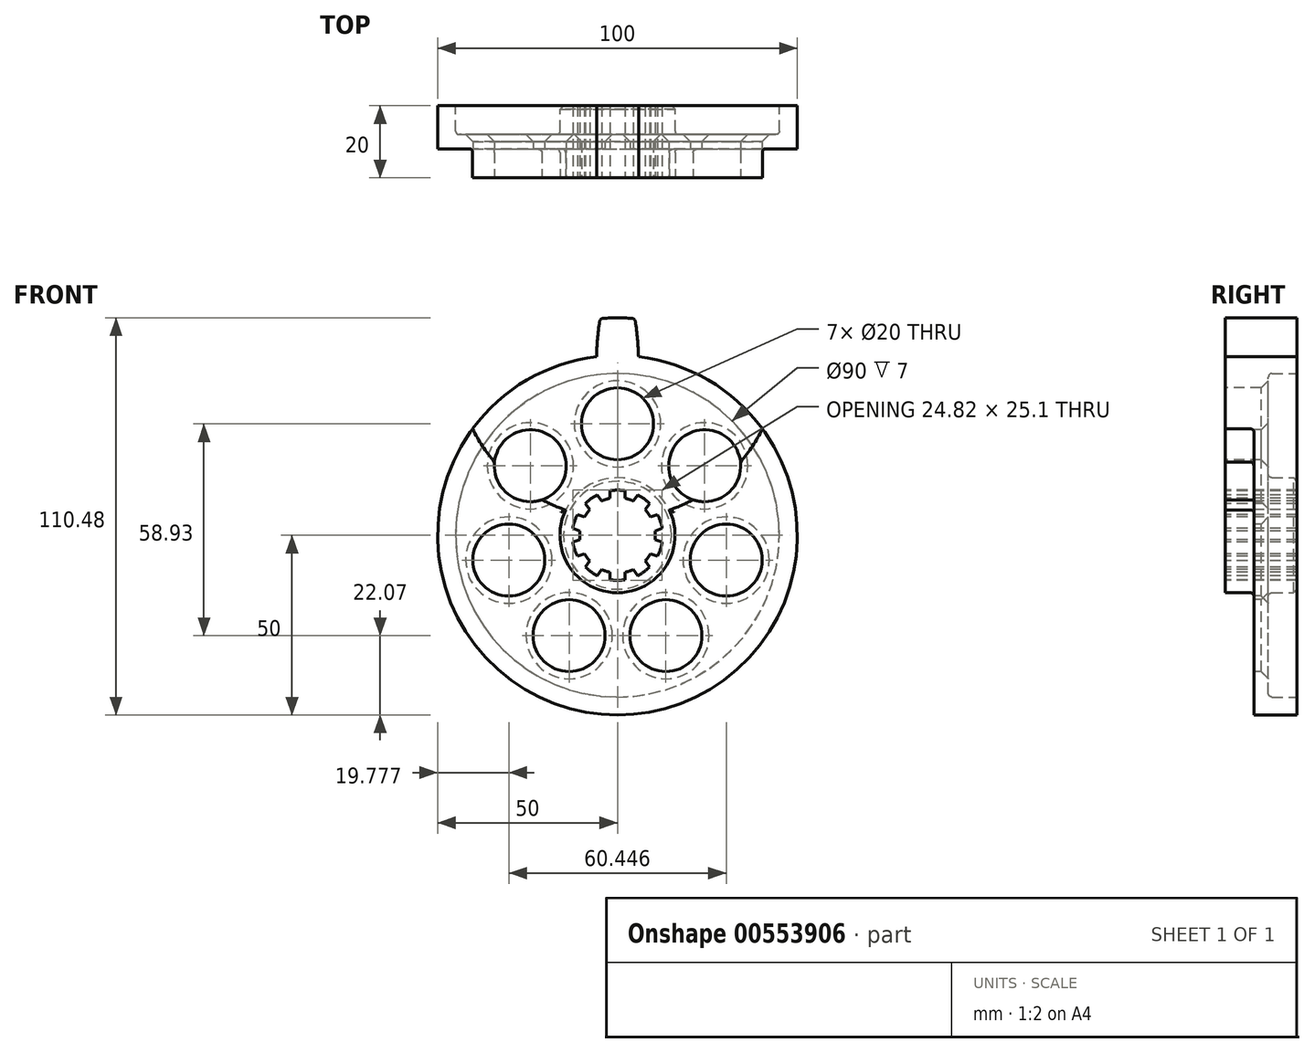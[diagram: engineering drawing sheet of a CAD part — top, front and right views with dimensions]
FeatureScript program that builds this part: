
annotation { "Feature Type Name" : "Feature", "Feature Type Description" : "" }
export const myFeature = defineFeature(function(context is Context, id is Id, definition is map)
    precondition{}
    {
        {
            var Q0;
            Q0=qCreatedBy(makeId("Front.planeOp"),FACE);
            var sketch = newSketch(context, id + "F0", { "sketchPlane" : qUnion([Q0])});
            skCircle(sketch, "E0", {"center": v(0, 0) * mm, "radius": 50 * mm});
            skLineSegment(sketch, "E1", {"start": v(-48.98, 46.5) * mm, "end": v(18.38, 46.5) * mm, "construction": true});
            skLineSegment(sketch, "E2", {"start": v(84.1, 97.1) * mm, "end": v(84.1, -36.75) * mm, "construction": true});
            skArc(sketch, "E3", {"start": v(-4.96, 59.5) * mm, "mid": v(-5.54, 54.59) * mm, "end": v(-5.84, 49.66) * mm});
            skArc(sketch, "E4.MirrorCS", {"start": v(4.96, 59.5) * mm, "mid": v(5.54, 54.59) * mm, "end": v(5.84, 49.66) * mm});
            skArc(sketch, "E5.trimOffspring", {"start": v(4.03, 60.35) * mm, "mid": v(0, 60.48) * mm, "end": v(-4.03, 60.35) * mm});
            skPoint(sketch, "E6.visualSharp", {"position": v(4.84, 60.29) * mm});
            skArc(sketch, "E6.filletArc", {"start": v(4.96, 59.5) * mm, "mid": v(4.65, 60.09) * mm, "end": v(4.03, 60.35) * mm});
            skPoint(sketch, "E7.visualSharp", {"position": v(-4.84, 60.29) * mm});
            skArc(sketch, "E7.filletArc", {"start": v(-4.03, 60.35) * mm, "mid": v(-4.65, 60.09) * mm, "end": v(-4.96, 59.5) * mm});
            skPoint(sketch, "E8.1.0", {"position": v(-54.63, -25.96) * mm});
            skArc(sketch, "E8.1.1", {"start": v(-54.28, -26.68) * mm, "mid": v(-52.38, -30.24) * mm, "end": v(-50.25, -33.67) * mm});
            skPoint(sketch, "E8.1.2", {"position": v(-49.8, -34.33) * mm});
            skArc(sketch, "E8.1.3", {"start": v(-54, -25.46) * mm, "mid": v(-50.04, -22.5) * mm, "end": v(-45.93, -19.77) * mm});
            skArc(sketch, "E8.1.4", {"start": v(-49.05, -34.04) * mm, "mid": v(-44.5, -32.09) * mm, "end": v(-40.08, -29.9) * mm});
            skArc(sketch, "E8.1.5", {"start": v(-50.25, -33.67) * mm, "mid": v(-49.71, -34.07) * mm, "end": v(-49.05, -34.04) * mm});
            skArc(sketch, "E8.1.6", {"start": v(-54, -25.46) * mm, "mid": v(-54.36, -26.02) * mm, "end": v(-54.28, -26.68) * mm});
            skPoint(sketch, "E8.2.0", {"position": v(49.8, -34.33) * mm});
            skArc(sketch, "E8.2.1", {"start": v(50.25, -33.67) * mm, "mid": v(52.38, -30.24) * mm, "end": v(54.28, -26.68) * mm});
            skPoint(sketch, "E8.2.2", {"position": v(54.63, -25.96) * mm});
            skArc(sketch, "E8.2.3", {"start": v(49.05, -34.04) * mm, "mid": v(44.5, -32.09) * mm, "end": v(40.08, -29.9) * mm});
            skArc(sketch, "E8.2.4", {"start": v(54, -25.46) * mm, "mid": v(50.04, -22.5) * mm, "end": v(45.93, -19.77) * mm});
            skArc(sketch, "E8.2.5", {"start": v(54.28, -26.68) * mm, "mid": v(54.36, -26.02) * mm, "end": v(54, -25.46) * mm});
            skArc(sketch, "E8.2.6", {"start": v(49.05, -34.04) * mm, "mid": v(49.71, -34.07) * mm, "end": v(50.25, -33.67) * mm});
            skSolve(sketch);
        }
        {
            var Q0;
            {var subQ0=sQuery(id+"F0.wireOp",EDGE,"E0");var subQ18=makeQuery(id+"F0.imprint","INTERSECT",VERTEX,{"derivedFrom":[subQ0,sQuery(id+"F0.wireOp",EDGE,"c62fa7f7-7299-4b17-82dd-0c70f37f38ce.11.0")]});Q0=makeQuery(id+"F0.imprint","IMPRINT",FACE,{"disambiguationData":[TD([[makeQuery(id+"F0.imprint","IMPRINT",EDGE,{"disambiguationData":[TD([[subQ18,-1.0]])],"derivedFrom":subQ0}),1.0]])]});}
            var Q1;
            {var subQ0=sQuery(id+"F0.wireOp",EDGE,"c62fa7f7-7299-4b17-82dd-0c70f37f38ce.1.0");Q1=makeQuery(id+"F0.imprint","IMPRINT",FACE,{"disambiguationData":[TD([[makeQuery(id+"F0.imprint","IMPRINT",EDGE,{"derivedFrom":subQ0}),1.0]])]});}
            var Q2;
            {var subQ0=sQuery(id+"F0.wireOp",EDGE,"E3");Q2=makeQuery(id+"F0.imprint","IMPRINT",FACE,{"disambiguationData":[TD([[makeQuery(id+"F0.imprint","IMPRINT",EDGE,{"derivedFrom":subQ0}),1.0]])]});}
            var Q3;
            {var subQ0=sQuery(id+"F0.wireOp",EDGE,"c62fa7f7-7299-4b17-82dd-0c70f37f38ce.14.0");Q3=makeQuery(id+"F0.imprint","IMPRINT",FACE,{"disambiguationData":[TD([[makeQuery(id+"F0.imprint","IMPRINT",EDGE,{"derivedFrom":subQ0}),1.0]])]});}
            var Q4;
            {var subQ0=sQuery(id+"F0.wireOp",EDGE,"c62fa7f7-7299-4b17-82dd-0c70f37f38ce.13.0");Q4=makeQuery(id+"F0.imprint","IMPRINT",FACE,{"disambiguationData":[TD([[makeQuery(id+"F0.imprint","IMPRINT",EDGE,{"derivedFrom":subQ0}),1.0]])]});}
            var Q5;
            {var subQ0=sQuery(id+"F0.wireOp",EDGE,"c62fa7f7-7299-4b17-82dd-0c70f37f38ce.12.0");Q5=makeQuery(id+"F0.imprint","IMPRINT",FACE,{"disambiguationData":[TD([[makeQuery(id+"F0.imprint","IMPRINT",EDGE,{"derivedFrom":subQ0}),1.0]])]});}
            var Q6;
            {var subQ0=sQuery(id+"F0.wireOp",EDGE,"c62fa7f7-7299-4b17-82dd-0c70f37f38ce.11.0");Q6=makeQuery(id+"F0.imprint","IMPRINT",FACE,{"disambiguationData":[TD([[makeQuery(id+"F0.imprint","IMPRINT",EDGE,{"derivedFrom":subQ0}),1.0]])]});}
            var Q7;
            {var subQ0=sQuery(id+"F0.wireOp",EDGE,"c62fa7f7-7299-4b17-82dd-0c70f37f38ce.10.0");Q7=makeQuery(id+"F0.imprint","IMPRINT",FACE,{"disambiguationData":[TD([[makeQuery(id+"F0.imprint","IMPRINT",EDGE,{"derivedFrom":subQ0}),1.0]])]});}
            var Q8;
            {var subQ0=sQuery(id+"F0.wireOp",EDGE,"c62fa7f7-7299-4b17-82dd-0c70f37f38ce.9.0");Q8=makeQuery(id+"F0.imprint","IMPRINT",FACE,{"disambiguationData":[TD([[makeQuery(id+"F0.imprint","IMPRINT",EDGE,{"derivedFrom":subQ0}),1.0]])]});}
            var Q9;
            {var subQ0=sQuery(id+"F0.wireOp",EDGE,"c62fa7f7-7299-4b17-82dd-0c70f37f38ce.8.0");Q9=makeQuery(id+"F0.imprint","IMPRINT",FACE,{"disambiguationData":[TD([[makeQuery(id+"F0.imprint","IMPRINT",EDGE,{"derivedFrom":subQ0}),1.0]])]});}
            var Q10;
            {var subQ0=sQuery(id+"F0.wireOp",EDGE,"c62fa7f7-7299-4b17-82dd-0c70f37f38ce.7.0");Q10=makeQuery(id+"F0.imprint","IMPRINT",FACE,{"disambiguationData":[TD([[makeQuery(id+"F0.imprint","IMPRINT",EDGE,{"derivedFrom":subQ0}),1.0]])]});}
            var Q11;
            {var subQ0=sQuery(id+"F0.wireOp",EDGE,"c62fa7f7-7299-4b17-82dd-0c70f37f38ce.6.0");Q11=makeQuery(id+"F0.imprint","IMPRINT",FACE,{"disambiguationData":[TD([[makeQuery(id+"F0.imprint","IMPRINT",EDGE,{"derivedFrom":subQ0}),1.0]])]});}
            var Q12;
            {var subQ0=sQuery(id+"F0.wireOp",EDGE,"c62fa7f7-7299-4b17-82dd-0c70f37f38ce.5.0");Q12=makeQuery(id+"F0.imprint","IMPRINT",FACE,{"disambiguationData":[TD([[makeQuery(id+"F0.imprint","IMPRINT",EDGE,{"derivedFrom":subQ0}),1.0]])]});}
            var Q13;
            {var subQ0=sQuery(id+"F0.wireOp",EDGE,"c62fa7f7-7299-4b17-82dd-0c70f37f38ce.4.0");Q13=makeQuery(id+"F0.imprint","IMPRINT",FACE,{"disambiguationData":[TD([[makeQuery(id+"F0.imprint","IMPRINT",EDGE,{"derivedFrom":subQ0}),1.0]])]});}
            var Q14;
            {var subQ0=sQuery(id+"F0.wireOp",EDGE,"c62fa7f7-7299-4b17-82dd-0c70f37f38ce.3.0");Q14=makeQuery(id+"F0.imprint","IMPRINT",FACE,{"disambiguationData":[TD([[makeQuery(id+"F0.imprint","IMPRINT",EDGE,{"derivedFrom":subQ0}),1.0]])]});}
            var Q15;
            {var subQ0=sQuery(id+"F0.wireOp",EDGE,"c62fa7f7-7299-4b17-82dd-0c70f37f38ce.2.0");Q15=makeQuery(id+"F0.imprint","IMPRINT",FACE,{"disambiguationData":[TD([[makeQuery(id+"F0.imprint","IMPRINT",EDGE,{"derivedFrom":subQ0}),1.0]])]});}
            extrude(context, id + "F1", {"entities" : qUnion([Q0, Q1, Q2, Q3, Q4, Q5, Q6, Q7, Q8, Q9, Q10, Q11, Q12, Q13, Q14, Q15]), "depth" : 20 * mm, "offsetDistance" : 25 * mm});
        }
        {
            var Q0;
            Q0=makeQuery(id+"F1.opExtrude","CAP_FACE",FACE,{"disambiguationData":[OSD([sQuery(id+"F0.wireOp",EDGE,"E0"),sQuery(id+"F0.wireOp",EDGE,"E3"),sQuery(id+"F0.wireOp",EDGE,"E4.MirrorCS"),sQuery(id+"F0.wireOp",EDGE,"E5.trimOffspring"),sQuery(id+"F0.wireOp",EDGE,"c62fa7f7-7299-4b17-82dd-0c70f37f38ce.1.0"),sQuery(id+"F0.wireOp",EDGE,"c62fa7f7-7299-4b17-82dd-0c70f37f38ce.1.1"),sQuery(id+"F0.wireOp",EDGE,"c62fa7f7-7299-4b17-82dd-0c70f37f38ce.1.2"),sQuery(id+"F0.wireOp",EDGE,"c62fa7f7-7299-4b17-82dd-0c70f37f38ce.2.0"),sQuery(id+"F0.wireOp",EDGE,"c62fa7f7-7299-4b17-82dd-0c70f37f38ce.2.1"),sQuery(id+"F0.wireOp",EDGE,"c62fa7f7-7299-4b17-82dd-0c70f37f38ce.2.2"),sQuery(id+"F0.wireOp",EDGE,"c62fa7f7-7299-4b17-82dd-0c70f37f38ce.3.0"),sQuery(id+"F0.wireOp",EDGE,"c62fa7f7-7299-4b17-82dd-0c70f37f38ce.3.1"),sQuery(id+"F0.wireOp",EDGE,"c62fa7f7-7299-4b17-82dd-0c70f37f38ce.3.2"),sQuery(id+"F0.wireOp",EDGE,"c62fa7f7-7299-4b17-82dd-0c70f37f38ce.4.0"),sQuery(id+"F0.wireOp",EDGE,"c62fa7f7-7299-4b17-82dd-0c70f37f38ce.4.1"),sQuery(id+"F0.wireOp",EDGE,"c62fa7f7-7299-4b17-82dd-0c70f37f38ce.4.2"),sQuery(id+"F0.wireOp",EDGE,"c62fa7f7-7299-4b17-82dd-0c70f37f38ce.5.0"),sQuery(id+"F0.wireOp",EDGE,"c62fa7f7-7299-4b17-82dd-0c70f37f38ce.5.1"),sQuery(id+"F0.wireOp",EDGE,"c62fa7f7-7299-4b17-82dd-0c70f37f38ce.5.2"),sQuery(id+"F0.wireOp",EDGE,"c62fa7f7-7299-4b17-82dd-0c70f37f38ce.6.0"),sQuery(id+"F0.wireOp",EDGE,"c62fa7f7-7299-4b17-82dd-0c70f37f38ce.6.1"),sQuery(id+"F0.wireOp",EDGE,"c62fa7f7-7299-4b17-82dd-0c70f37f38ce.6.2"),sQuery(id+"F0.wireOp",EDGE,"c62fa7f7-7299-4b17-82dd-0c70f37f38ce.7.0"),sQuery(id+"F0.wireOp",EDGE,"c62fa7f7-7299-4b17-82dd-0c70f37f38ce.7.1"),sQuery(id+"F0.wireOp",EDGE,"c62fa7f7-7299-4b17-82dd-0c70f37f38ce.7.2"),sQuery(id+"F0.wireOp",EDGE,"c62fa7f7-7299-4b17-82dd-0c70f37f38ce.8.0"),sQuery(id+"F0.wireOp",EDGE,"c62fa7f7-7299-4b17-82dd-0c70f37f38ce.8.1"),sQuery(id+"F0.wireOp",EDGE,"c62fa7f7-7299-4b17-82dd-0c70f37f38ce.8.2"),sQuery(id+"F0.wireOp",EDGE,"c62fa7f7-7299-4b17-82dd-0c70f37f38ce.9.0"),sQuery(id+"F0.wireOp",EDGE,"c62fa7f7-7299-4b17-82dd-0c70f37f38ce.9.1"),sQuery(id+"F0.wireOp",EDGE,"c62fa7f7-7299-4b17-82dd-0c70f37f38ce.9.2"),sQuery(id+"F0.wireOp",EDGE,"c62fa7f7-7299-4b17-82dd-0c70f37f38ce.10.0"),sQuery(id+"F0.wireOp",EDGE,"c62fa7f7-7299-4b17-82dd-0c70f37f38ce.10.1"),sQuery(id+"F0.wireOp",EDGE,"c62fa7f7-7299-4b17-82dd-0c70f37f38ce.10.2"),sQuery(id+"F0.wireOp",EDGE,"c62fa7f7-7299-4b17-82dd-0c70f37f38ce.11.0"),sQuery(id+"F0.wireOp",EDGE,"c62fa7f7-7299-4b17-82dd-0c70f37f38ce.11.1"),sQuery(id+"F0.wireOp",EDGE,"c62fa7f7-7299-4b17-82dd-0c70f37f38ce.11.2"),sQuery(id+"F0.wireOp",EDGE,"c62fa7f7-7299-4b17-82dd-0c70f37f38ce.12.0"),sQuery(id+"F0.wireOp",EDGE,"c62fa7f7-7299-4b17-82dd-0c70f37f38ce.12.1"),sQuery(id+"F0.wireOp",EDGE,"c62fa7f7-7299-4b17-82dd-0c70f37f38ce.12.2"),sQuery(id+"F0.wireOp",EDGE,"c62fa7f7-7299-4b17-82dd-0c70f37f38ce.13.0"),sQuery(id+"F0.wireOp",EDGE,"c62fa7f7-7299-4b17-82dd-0c70f37f38ce.13.1"),sQuery(id+"F0.wireOp",EDGE,"c62fa7f7-7299-4b17-82dd-0c70f37f38ce.13.2"),sQuery(id+"F0.wireOp",EDGE,"c62fa7f7-7299-4b17-82dd-0c70f37f38ce.14.0"),sQuery(id+"F0.wireOp",EDGE,"c62fa7f7-7299-4b17-82dd-0c70f37f38ce.14.1"),sQuery(id+"F0.wireOp",EDGE,"c62fa7f7-7299-4b17-82dd-0c70f37f38ce.14.2")])],"isStart":false});
            var sketch = newSketch(context, id + "F2", { "sketchPlane" : qUnion([Q0])});
            skCircle(sketch, "E9", {"center": v(0, 0) * mm, "radius": 10.5 * mm});
            skArc(sketch, "E10", {"start": v(2.05, 12.38) * mm, "mid": v(0, 12.55) * mm, "end": v(-2.05, 12.38) * mm});
            skLineSegment(sketch, "E11", {"start": v(-2.05, 12.38) * mm, "end": v(-2.05, 10.3) * mm});
            skLineSegment(sketch, "E12", {"start": v(2.05, 12.38) * mm, "end": v(2.05, 10.3) * mm});
            skLineSegment(sketch, "E13.1.0", {"start": v(-8.94, 8.81) * mm, "end": v(-7.71, 7.13) * mm});
            skArc(sketch, "E13.1.1", {"start": v(-5.62, 11.22) * mm, "mid": v(-7.38, 10.15) * mm, "end": v(-8.94, 8.81) * mm});
            skLineSegment(sketch, "E13.1.2", {"start": v(-5.62, 11.22) * mm, "end": v(-4.4, 9.54) * mm});
            skLineSegment(sketch, "E13.2.0", {"start": v(-12.4, 1.88) * mm, "end": v(-10.43, 1.23) * mm});
            skArc(sketch, "E13.2.1", {"start": v(-11.14, 5.78) * mm, "mid": v(-11.94, 3.88) * mm, "end": v(-12.4, 1.88) * mm});
            skLineSegment(sketch, "E13.2.2", {"start": v(-11.14, 5.78) * mm, "end": v(-9.16, 5.13) * mm});
            skLineSegment(sketch, "E13.3.0", {"start": v(-11.14, -5.78) * mm, "end": v(-9.16, -5.13) * mm});
            skArc(sketch, "E13.3.1", {"start": v(-12.4, -1.88) * mm, "mid": v(-11.94, -3.88) * mm, "end": v(-11.14, -5.78) * mm});
            skLineSegment(sketch, "E13.3.2", {"start": v(-12.4, -1.88) * mm, "end": v(-10.43, -1.23) * mm});
            skLineSegment(sketch, "E13.4.0", {"start": v(-5.62, -11.22) * mm, "end": v(-4.4, -9.54) * mm});
            skArc(sketch, "E13.4.1", {"start": v(-8.94, -8.81) * mm, "mid": v(-7.38, -10.15) * mm, "end": v(-5.62, -11.22) * mm});
            skLineSegment(sketch, "E13.4.2", {"start": v(-8.94, -8.81) * mm, "end": v(-7.71, -7.13) * mm});
            skLineSegment(sketch, "E13.5.0", {"start": v(2.05, -12.38) * mm, "end": v(2.05, -10.3) * mm});
            skArc(sketch, "E13.5.1", {"start": v(-2.05, -12.38) * mm, "mid": v(0, -12.55) * mm, "end": v(2.05, -12.38) * mm});
            skLineSegment(sketch, "E13.5.2", {"start": v(-2.05, -12.38) * mm, "end": v(-2.05, -10.3) * mm});
            skLineSegment(sketch, "E13.6.0", {"start": v(8.94, -8.81) * mm, "end": v(7.71, -7.13) * mm});
            skArc(sketch, "E13.6.1", {"start": v(5.62, -11.22) * mm, "mid": v(7.38, -10.15) * mm, "end": v(8.94, -8.81) * mm});
            skLineSegment(sketch, "E13.6.2", {"start": v(5.62, -11.22) * mm, "end": v(4.4, -9.54) * mm});
            skLineSegment(sketch, "E13.7.0", {"start": v(12.4, -1.88) * mm, "end": v(10.43, -1.23) * mm});
            skArc(sketch, "E13.7.1", {"start": v(11.14, -5.78) * mm, "mid": v(11.94, -3.88) * mm, "end": v(12.4, -1.88) * mm});
            skLineSegment(sketch, "E13.7.2", {"start": v(11.14, -5.78) * mm, "end": v(9.16, -5.13) * mm});
            skLineSegment(sketch, "E13.8.0", {"start": v(11.14, 5.78) * mm, "end": v(9.16, 5.13) * mm});
            skArc(sketch, "E13.8.1", {"start": v(12.4, 1.88) * mm, "mid": v(11.94, 3.88) * mm, "end": v(11.14, 5.78) * mm});
            skLineSegment(sketch, "E13.8.2", {"start": v(12.4, 1.88) * mm, "end": v(10.43, 1.23) * mm});
            skLineSegment(sketch, "E13.9.0", {"start": v(5.62, 11.22) * mm, "end": v(4.4, 9.54) * mm});
            skArc(sketch, "E13.9.1", {"start": v(8.94, 8.81) * mm, "mid": v(7.38, 10.15) * mm, "end": v(5.62, 11.22) * mm});
            skLineSegment(sketch, "E13.9.2", {"start": v(8.94, 8.81) * mm, "end": v(7.71, 7.13) * mm});
            skSolve(sketch);
        }
        {
            var Q0;
            {var subQ0=sQuery(id+"F2.wireOp",EDGE,"E9");var subQ8=makeQuery(id+"F2.imprint","INTERSECT",VERTEX,{"derivedFrom":[subQ0,sQuery(id+"F2.wireOp",EDGE,"E13.8.0")]});Q0=makeQuery(id+"F2.imprint","IMPRINT",FACE,{"disambiguationData":[TD([[makeQuery(id+"F2.imprint","IMPRINT",EDGE,{"disambiguationData":[TD([[subQ8,1.0]])],"derivedFrom":subQ0}),1.0]])]});}
            var Q1;
            {var subQ0=sQuery(id+"F2.wireOp",EDGE,"E13.1.0");Q1=makeQuery(id+"F2.imprint","IMPRINT",FACE,{"disambiguationData":[TD([[makeQuery(id+"F2.imprint","IMPRINT",EDGE,{"derivedFrom":subQ0}),1.0]])]});}
            var Q2;
            Q2=makeQuery(id+"F2.imprint","IMPRINT",FACE,{"disambiguationData":[TD([[makeQuery(id+"F2.imprint","IMPRINT",EDGE,{"derivedFrom":sQuery(id+"F2.wireOp",EDGE,"E10")}),1.0]])]});
            var Q3;
            {var subQ0=sQuery(id+"F2.wireOp",EDGE,"E13.9.0");Q3=makeQuery(id+"F2.imprint","IMPRINT",FACE,{"disambiguationData":[TD([[makeQuery(id+"F2.imprint","IMPRINT",EDGE,{"derivedFrom":subQ0}),1.0]])]});}
            var Q4;
            {var subQ0=sQuery(id+"F2.wireOp",EDGE,"E13.2.0");Q4=makeQuery(id+"F2.imprint","IMPRINT",FACE,{"disambiguationData":[TD([[makeQuery(id+"F2.imprint","IMPRINT",EDGE,{"derivedFrom":subQ0}),1.0]])]});}
            var Q5;
            {var subQ0=sQuery(id+"F2.wireOp",EDGE,"E13.3.0");Q5=makeQuery(id+"F2.imprint","IMPRINT",FACE,{"disambiguationData":[TD([[makeQuery(id+"F2.imprint","IMPRINT",EDGE,{"derivedFrom":subQ0}),1.0]])]});}
            var Q6;
            {var subQ0=sQuery(id+"F2.wireOp",EDGE,"E13.4.0");Q6=makeQuery(id+"F2.imprint","IMPRINT",FACE,{"disambiguationData":[TD([[makeQuery(id+"F2.imprint","IMPRINT",EDGE,{"derivedFrom":subQ0}),1.0]])]});}
            var Q7;
            {var subQ0=sQuery(id+"F2.wireOp",EDGE,"E13.5.0");Q7=makeQuery(id+"F2.imprint","IMPRINT",FACE,{"disambiguationData":[TD([[makeQuery(id+"F2.imprint","IMPRINT",EDGE,{"derivedFrom":subQ0}),1.0]])]});}
            var Q8;
            {var subQ0=sQuery(id+"F2.wireOp",EDGE,"E13.6.0");Q8=makeQuery(id+"F2.imprint","IMPRINT",FACE,{"disambiguationData":[TD([[makeQuery(id+"F2.imprint","IMPRINT",EDGE,{"derivedFrom":subQ0}),1.0]])]});}
            var Q9;
            {var subQ0=sQuery(id+"F2.wireOp",EDGE,"E13.7.0");Q9=makeQuery(id+"F2.imprint","IMPRINT",FACE,{"disambiguationData":[TD([[makeQuery(id+"F2.imprint","IMPRINT",EDGE,{"derivedFrom":subQ0}),1.0]])]});}
            var Q10;
            {var subQ0=sQuery(id+"F2.wireOp",EDGE,"E13.8.0");Q10=makeQuery(id+"F2.imprint","IMPRINT",FACE,{"disambiguationData":[TD([[makeQuery(id+"F2.imprint","IMPRINT",EDGE,{"derivedFrom":subQ0}),1.0]])]});}
            extrude(context, id + "F3", {"entities" : qUnion([Q0, Q1, Q2, Q3, Q4, Q5, Q6, Q7, Q8, Q9, Q10]), "operationType" : NewBodyOperationType.REMOVE, "oppositeDirection" : true, "depth" : 20 * mm, "offsetDistance" : 25 * mm});
        }
        {
            var Q0;
            Q0=makeQuery(id+"F1.opExtrude","CAP_FACE",FACE,{"disambiguationData":[OSD([sQuery(id+"F0.wireOp",EDGE,"E0"),sQuery(id+"F0.wireOp",EDGE,"E3"),sQuery(id+"F0.wireOp",EDGE,"E4.MirrorCS"),sQuery(id+"F0.wireOp",EDGE,"E5.trimOffspring"),sQuery(id+"F0.wireOp",EDGE,"c62fa7f7-7299-4b17-82dd-0c70f37f38ce.1.0"),sQuery(id+"F0.wireOp",EDGE,"c62fa7f7-7299-4b17-82dd-0c70f37f38ce.1.1"),sQuery(id+"F0.wireOp",EDGE,"c62fa7f7-7299-4b17-82dd-0c70f37f38ce.1.2"),sQuery(id+"F0.wireOp",EDGE,"c62fa7f7-7299-4b17-82dd-0c70f37f38ce.2.0"),sQuery(id+"F0.wireOp",EDGE,"c62fa7f7-7299-4b17-82dd-0c70f37f38ce.2.1"),sQuery(id+"F0.wireOp",EDGE,"c62fa7f7-7299-4b17-82dd-0c70f37f38ce.2.2"),sQuery(id+"F0.wireOp",EDGE,"c62fa7f7-7299-4b17-82dd-0c70f37f38ce.3.0"),sQuery(id+"F0.wireOp",EDGE,"c62fa7f7-7299-4b17-82dd-0c70f37f38ce.3.1"),sQuery(id+"F0.wireOp",EDGE,"c62fa7f7-7299-4b17-82dd-0c70f37f38ce.3.2"),sQuery(id+"F0.wireOp",EDGE,"c62fa7f7-7299-4b17-82dd-0c70f37f38ce.4.0"),sQuery(id+"F0.wireOp",EDGE,"c62fa7f7-7299-4b17-82dd-0c70f37f38ce.4.1"),sQuery(id+"F0.wireOp",EDGE,"c62fa7f7-7299-4b17-82dd-0c70f37f38ce.4.2"),sQuery(id+"F0.wireOp",EDGE,"c62fa7f7-7299-4b17-82dd-0c70f37f38ce.5.0"),sQuery(id+"F0.wireOp",EDGE,"c62fa7f7-7299-4b17-82dd-0c70f37f38ce.5.1"),sQuery(id+"F0.wireOp",EDGE,"c62fa7f7-7299-4b17-82dd-0c70f37f38ce.5.2"),sQuery(id+"F0.wireOp",EDGE,"c62fa7f7-7299-4b17-82dd-0c70f37f38ce.6.0"),sQuery(id+"F0.wireOp",EDGE,"c62fa7f7-7299-4b17-82dd-0c70f37f38ce.6.1"),sQuery(id+"F0.wireOp",EDGE,"c62fa7f7-7299-4b17-82dd-0c70f37f38ce.6.2"),sQuery(id+"F0.wireOp",EDGE,"c62fa7f7-7299-4b17-82dd-0c70f37f38ce.7.0"),sQuery(id+"F0.wireOp",EDGE,"c62fa7f7-7299-4b17-82dd-0c70f37f38ce.7.1"),sQuery(id+"F0.wireOp",EDGE,"c62fa7f7-7299-4b17-82dd-0c70f37f38ce.7.2"),sQuery(id+"F0.wireOp",EDGE,"c62fa7f7-7299-4b17-82dd-0c70f37f38ce.8.0"),sQuery(id+"F0.wireOp",EDGE,"c62fa7f7-7299-4b17-82dd-0c70f37f38ce.8.1"),sQuery(id+"F0.wireOp",EDGE,"c62fa7f7-7299-4b17-82dd-0c70f37f38ce.8.2"),sQuery(id+"F0.wireOp",EDGE,"c62fa7f7-7299-4b17-82dd-0c70f37f38ce.9.0"),sQuery(id+"F0.wireOp",EDGE,"c62fa7f7-7299-4b17-82dd-0c70f37f38ce.9.1"),sQuery(id+"F0.wireOp",EDGE,"c62fa7f7-7299-4b17-82dd-0c70f37f38ce.9.2"),sQuery(id+"F0.wireOp",EDGE,"c62fa7f7-7299-4b17-82dd-0c70f37f38ce.10.0"),sQuery(id+"F0.wireOp",EDGE,"c62fa7f7-7299-4b17-82dd-0c70f37f38ce.10.1"),sQuery(id+"F0.wireOp",EDGE,"c62fa7f7-7299-4b17-82dd-0c70f37f38ce.10.2"),sQuery(id+"F0.wireOp",EDGE,"c62fa7f7-7299-4b17-82dd-0c70f37f38ce.11.0"),sQuery(id+"F0.wireOp",EDGE,"c62fa7f7-7299-4b17-82dd-0c70f37f38ce.11.1"),sQuery(id+"F0.wireOp",EDGE,"c62fa7f7-7299-4b17-82dd-0c70f37f38ce.11.2"),sQuery(id+"F0.wireOp",EDGE,"c62fa7f7-7299-4b17-82dd-0c70f37f38ce.12.0"),sQuery(id+"F0.wireOp",EDGE,"c62fa7f7-7299-4b17-82dd-0c70f37f38ce.12.1"),sQuery(id+"F0.wireOp",EDGE,"c62fa7f7-7299-4b17-82dd-0c70f37f38ce.12.2"),sQuery(id+"F0.wireOp",EDGE,"c62fa7f7-7299-4b17-82dd-0c70f37f38ce.13.0"),sQuery(id+"F0.wireOp",EDGE,"c62fa7f7-7299-4b17-82dd-0c70f37f38ce.13.1"),sQuery(id+"F0.wireOp",EDGE,"c62fa7f7-7299-4b17-82dd-0c70f37f38ce.13.2"),sQuery(id+"F0.wireOp",EDGE,"c62fa7f7-7299-4b17-82dd-0c70f37f38ce.14.0"),sQuery(id+"F0.wireOp",EDGE,"c62fa7f7-7299-4b17-82dd-0c70f37f38ce.14.1"),sQuery(id+"F0.wireOp",EDGE,"c62fa7f7-7299-4b17-82dd-0c70f37f38ce.14.2")])],"isStart":false});
            var sketch = newSketch(context, id + "F4", { "sketchPlane" : qUnion([Q0])});
            skCircle(sketch, "E14", {"center": v(0, 31) * mm, "radius": 10 * mm});
            skCircle(sketch, "E15.1.0", {"center": v(-24.24, 19.33) * mm, "radius": 10 * mm});
            skCircle(sketch, "E15.2.0", {"center": v(-30.22, -6.9) * mm, "radius": 10 * mm});
            skCircle(sketch, "E15.3.0", {"center": v(-13.45, -27.93) * mm, "radius": 10 * mm});
            skCircle(sketch, "E15.4.0", {"center": v(13.45, -27.93) * mm, "radius": 10 * mm});
            skCircle(sketch, "E15.5.0", {"center": v(30.22, -6.9) * mm, "radius": 10 * mm});
            skCircle(sketch, "E15.6.0", {"center": v(24.24, 19.33) * mm, "radius": 10 * mm});
            skPoint(sketch, "E15.center", {"position": v(0, 0) * mm});
            skSolve(sketch);
        }
        {
            var Q0;
            Q0=makeQuery(id+"F4.imprint","IMPRINT",FACE,{"disambiguationData":[TD([[makeQuery(id+"F4.imprint","IMPRINT",EDGE,{"derivedFrom":sQuery(id+"F4.wireOp",EDGE,"E15.1.0")}),1.0]])]});
            var Q1;
            Q1=makeQuery(id+"F4.imprint","IMPRINT",FACE,{"disambiguationData":[TD([[makeQuery(id+"F4.imprint","IMPRINT",EDGE,{"derivedFrom":sQuery(id+"F4.wireOp",EDGE,"E14")}),1.0]])]});
            var Q2;
            Q2=makeQuery(id+"F4.imprint","IMPRINT",FACE,{"disambiguationData":[TD([[makeQuery(id+"F4.imprint","IMPRINT",EDGE,{"derivedFrom":sQuery(id+"F4.wireOp",EDGE,"E15.6.0")}),1.0]])]});
            var Q3;
            Q3=makeQuery(id+"F4.imprint","IMPRINT",FACE,{"disambiguationData":[TD([[makeQuery(id+"F4.imprint","IMPRINT",EDGE,{"derivedFrom":sQuery(id+"F4.wireOp",EDGE,"E15.5.0")}),1.0]])]});
            var Q4;
            Q4=makeQuery(id+"F4.imprint","IMPRINT",FACE,{"disambiguationData":[TD([[makeQuery(id+"F4.imprint","IMPRINT",EDGE,{"derivedFrom":sQuery(id+"F4.wireOp",EDGE,"E15.4.0")}),1.0]])]});
            var Q5;
            Q5=makeQuery(id+"F4.imprint","IMPRINT",FACE,{"disambiguationData":[TD([[makeQuery(id+"F4.imprint","IMPRINT",EDGE,{"derivedFrom":sQuery(id+"F4.wireOp",EDGE,"E15.3.0")}),1.0]])]});
            var Q6;
            Q6=makeQuery(id+"F4.imprint","IMPRINT",FACE,{"disambiguationData":[TD([[makeQuery(id+"F4.imprint","IMPRINT",EDGE,{"derivedFrom":sQuery(id+"F4.wireOp",EDGE,"E15.2.0")}),1.0]])]});
            var Q7;
            Q7=sQuery(id+"F4.wireOp",EDGE,"E14");
            var Q8;
            Q8=sQuery(id+"F4.wireOp",EDGE,"E15.1.0");
            var Q9;
            Q9=sQuery(id+"F4.wireOp",EDGE,"E15.2.0");
            var Q10;
            Q10=sQuery(id+"F4.wireOp",EDGE,"E15.3.0");
            var Q11;
            Q11=sQuery(id+"F4.wireOp",EDGE,"E15.4.0");
            var Q12;
            Q12=sQuery(id+"F4.wireOp",EDGE,"E15.5.0");
            var Q13;
            Q13=sQuery(id+"F4.wireOp",EDGE,"E15.6.0");
            extrude(context, id + "F5", {"entities" : qUnion([Q0, Q1, Q2, Q3, Q4, Q5, Q6]), "operationType" : NewBodyOperationType.REMOVE, "surfaceEntities" : qUnion([Q7, Q8, Q9, Q10, Q11, Q12, Q13]), "endBound" : BoundingType.THROUGH_ALL, "oppositeDirection" : true, "depth" : mm, "offsetDistance" : 25 * mm});
        }
        {
            var Q0;
            Q0=makeQuery(id+"F1.opExtrude","CAP_FACE",FACE,{"disambiguationData":[OSD([sQuery(id+"F0.wireOp",EDGE,"E0"),sQuery(id+"F0.wireOp",EDGE,"E3"),sQuery(id+"F0.wireOp",EDGE,"E4.MirrorCS"),sQuery(id+"F0.wireOp",EDGE,"E5.trimOffspring"),sQuery(id+"F0.wireOp",EDGE,"c62fa7f7-7299-4b17-82dd-0c70f37f38ce.1.0"),sQuery(id+"F0.wireOp",EDGE,"c62fa7f7-7299-4b17-82dd-0c70f37f38ce.1.1"),sQuery(id+"F0.wireOp",EDGE,"c62fa7f7-7299-4b17-82dd-0c70f37f38ce.1.2"),sQuery(id+"F0.wireOp",EDGE,"c62fa7f7-7299-4b17-82dd-0c70f37f38ce.2.0"),sQuery(id+"F0.wireOp",EDGE,"c62fa7f7-7299-4b17-82dd-0c70f37f38ce.2.1"),sQuery(id+"F0.wireOp",EDGE,"c62fa7f7-7299-4b17-82dd-0c70f37f38ce.2.2"),sQuery(id+"F0.wireOp",EDGE,"c62fa7f7-7299-4b17-82dd-0c70f37f38ce.3.0"),sQuery(id+"F0.wireOp",EDGE,"c62fa7f7-7299-4b17-82dd-0c70f37f38ce.3.1"),sQuery(id+"F0.wireOp",EDGE,"c62fa7f7-7299-4b17-82dd-0c70f37f38ce.3.2"),sQuery(id+"F0.wireOp",EDGE,"c62fa7f7-7299-4b17-82dd-0c70f37f38ce.4.0"),sQuery(id+"F0.wireOp",EDGE,"c62fa7f7-7299-4b17-82dd-0c70f37f38ce.4.1"),sQuery(id+"F0.wireOp",EDGE,"c62fa7f7-7299-4b17-82dd-0c70f37f38ce.4.2"),sQuery(id+"F0.wireOp",EDGE,"c62fa7f7-7299-4b17-82dd-0c70f37f38ce.5.0"),sQuery(id+"F0.wireOp",EDGE,"c62fa7f7-7299-4b17-82dd-0c70f37f38ce.5.1"),sQuery(id+"F0.wireOp",EDGE,"c62fa7f7-7299-4b17-82dd-0c70f37f38ce.5.2"),sQuery(id+"F0.wireOp",EDGE,"c62fa7f7-7299-4b17-82dd-0c70f37f38ce.6.0"),sQuery(id+"F0.wireOp",EDGE,"c62fa7f7-7299-4b17-82dd-0c70f37f38ce.6.1"),sQuery(id+"F0.wireOp",EDGE,"c62fa7f7-7299-4b17-82dd-0c70f37f38ce.6.2"),sQuery(id+"F0.wireOp",EDGE,"c62fa7f7-7299-4b17-82dd-0c70f37f38ce.7.0"),sQuery(id+"F0.wireOp",EDGE,"c62fa7f7-7299-4b17-82dd-0c70f37f38ce.7.1"),sQuery(id+"F0.wireOp",EDGE,"c62fa7f7-7299-4b17-82dd-0c70f37f38ce.7.2"),sQuery(id+"F0.wireOp",EDGE,"c62fa7f7-7299-4b17-82dd-0c70f37f38ce.8.0"),sQuery(id+"F0.wireOp",EDGE,"c62fa7f7-7299-4b17-82dd-0c70f37f38ce.8.1"),sQuery(id+"F0.wireOp",EDGE,"c62fa7f7-7299-4b17-82dd-0c70f37f38ce.8.2"),sQuery(id+"F0.wireOp",EDGE,"c62fa7f7-7299-4b17-82dd-0c70f37f38ce.9.0"),sQuery(id+"F0.wireOp",EDGE,"c62fa7f7-7299-4b17-82dd-0c70f37f38ce.9.1"),sQuery(id+"F0.wireOp",EDGE,"c62fa7f7-7299-4b17-82dd-0c70f37f38ce.9.2"),sQuery(id+"F0.wireOp",EDGE,"c62fa7f7-7299-4b17-82dd-0c70f37f38ce.10.0"),sQuery(id+"F0.wireOp",EDGE,"c62fa7f7-7299-4b17-82dd-0c70f37f38ce.10.1"),sQuery(id+"F0.wireOp",EDGE,"c62fa7f7-7299-4b17-82dd-0c70f37f38ce.10.2"),sQuery(id+"F0.wireOp",EDGE,"c62fa7f7-7299-4b17-82dd-0c70f37f38ce.11.0"),sQuery(id+"F0.wireOp",EDGE,"c62fa7f7-7299-4b17-82dd-0c70f37f38ce.11.1"),sQuery(id+"F0.wireOp",EDGE,"c62fa7f7-7299-4b17-82dd-0c70f37f38ce.11.2"),sQuery(id+"F0.wireOp",EDGE,"c62fa7f7-7299-4b17-82dd-0c70f37f38ce.12.0"),sQuery(id+"F0.wireOp",EDGE,"c62fa7f7-7299-4b17-82dd-0c70f37f38ce.12.1"),sQuery(id+"F0.wireOp",EDGE,"c62fa7f7-7299-4b17-82dd-0c70f37f38ce.12.2"),sQuery(id+"F0.wireOp",EDGE,"c62fa7f7-7299-4b17-82dd-0c70f37f38ce.13.0"),sQuery(id+"F0.wireOp",EDGE,"c62fa7f7-7299-4b17-82dd-0c70f37f38ce.13.1"),sQuery(id+"F0.wireOp",EDGE,"c62fa7f7-7299-4b17-82dd-0c70f37f38ce.13.2"),sQuery(id+"F0.wireOp",EDGE,"c62fa7f7-7299-4b17-82dd-0c70f37f38ce.14.0"),sQuery(id+"F0.wireOp",EDGE,"c62fa7f7-7299-4b17-82dd-0c70f37f38ce.14.1"),sQuery(id+"F0.wireOp",EDGE,"c62fa7f7-7299-4b17-82dd-0c70f37f38ce.14.2")])],"isStart":false});
            var sketch = newSketch(context, id + "F6", { "sketchPlane" : qUnion([Q0])});
            skCircle(sketch, "E16", {"center": v(0, 0) * mm, "radius": 16 * mm});
            skCircle(sketch, "E17", {"center": v(0, 49.66) * mm, "radius": 45 * mm});
            skSolve(sketch);
        }
        {
            var Q0;
            Q0=makeQuery(id+"F6.imprint","IMPRINT",FACE,{"disambiguationData":[TD([[makeQuery(id+"F6.imprint","IMPRINT",EDGE,{"derivedFrom":sQuery(id+"F6.wireOp",EDGE,"E16")}),-1.0]])]});
            extrude(context, id + "F7", {"entities" : qUnion([Q0]), "operationType" : NewBodyOperationType.REMOVE, "oppositeDirection" : true, "depth" : 8 * mm, "offsetDistance" : 25 * mm});
        }
        {
            var Q0;
            Q0=qCreatedBy(makeId("Right.planeOp"),FACE);
            var sketch = newSketch(context, id + "F8", { "sketchPlane" : qUnion([Q0])});
            skLineSegment(sketch, "E18.bottom", {"start": v(-8, 45) * mm, "end": v(0, 45) * mm});
            skLineSegment(sketch, "E18.top", {"start": v(-8, 16) * mm, "end": v(0, 16) * mm});
            skLineSegment(sketch, "E18.left", {"start": v(-8, 45) * mm, "end": v(-8, 16) * mm});
            skLineSegment(sketch, "E18.right", {"start": v(0, 45) * mm, "end": v(0, 16) * mm});
            skLineSegment(sketch, "E19", {"start": v(-39.76, 0) * mm, "end": v(30.47, 0) * mm, "construction": true});
            skSolve(sketch);
        }
        {
            var Q0;
            Q0=makeQuery(id+"F8.imprint","IMPRINT",FACE,{"disambiguationData":[TD([[makeQuery(id+"F8.imprint","IMPRINT",EDGE,{"derivedFrom":sQuery(id+"F8.wireOp",EDGE,"E18.bottom")}),-1.0]])]});
            var Q1;
            Q1=sQuery(id+"F8.wireOp",EDGE,"E19");
            revolve(context, id + "F9", {"operationType" : NewBodyOperationType.REMOVE, "entities" : qUnion([Q0]), "axis" : qUnion([Q1]), "revolveType" : RevolveType.FULL, "oppositeDirection" : true});
        }
        {
            var Q0;
            Q0=makeQuery(id+"F7.boolean.opBoolean","COPY",EDGE,{"derivedFrom":makeQuery(id+"F7.opExtrude","CAP_EDGE",EDGE,{"disambiguationData":[OSD([sQuery(id+"F6.wireOp",EDGE,"E17")])],"isStart":false})});
            var Q1;
            Q1=makeQuery(id+"F7.boolean.opBoolean","COPY",EDGE,{"derivedFrom":makeQuery(id+"F7.opExtrude","CAP_EDGE",EDGE,{"disambiguationData":[OSD([sQuery(id+"F6.wireOp",EDGE,"E16")])],"isStart":false})});
            var Q2;
            Q2=makeQuery(id+"F9.boolean.opBoolean","COPY",EDGE,{"derivedFrom":makeQuery(id+"F9.opRevolve","SWEPT_EDGE",EDGE,{"disambiguationData":[OSD([sQuery(id+"F8.wireOp",EDGE,"E18.bottom"),sQuery(id+"F8.wireOp",EDGE,"E18.left")])]})});
            var Q3;
            Q3=makeQuery(id+"F9.boolean.opBoolean","COPY",EDGE,{"derivedFrom":makeQuery(id+"F9.opRevolve","SWEPT_EDGE",EDGE,{"disambiguationData":[OSD([sQuery(id+"F8.wireOp",EDGE,"E18.top"),sQuery(id+"F8.wireOp",EDGE,"E18.left")])]})});
            fillet(context, id + "F10", {"entities" : qUnion([Q0, Q1, Q2, Q3]), "radius" : 1 * mm, "tangentPropagation" : true, "allowEdgeOverflow" : false});
        }
        {
            var Q0;
            Q0=makeQuery(id+"F7.boolean.opBoolean","COPY",EDGE,{"derivedFrom":makeQuery(id+"F7.opExtrude","CAP_EDGE",EDGE,{"disambiguationData":[OSD([sQuery(id+"F6.wireOp",EDGE,"E17")])],"isStart":true})});
            var Q1;
            Q1=makeQuery(id+"F7.boolean.opBoolean","COPY",EDGE,{"derivedFrom":makeQuery(id+"F7.opExtrude","CAP_EDGE",EDGE,{"disambiguationData":[OSD([sQuery(id+"F6.wireOp",EDGE,"E16")])],"isStart":true})});
            var Q2;
            Q2=makeQuery(id+"F9.boolean.opBoolean","COPY",EDGE,{"derivedFrom":makeQuery(id+"F9.opRevolve","SWEPT_EDGE",EDGE,{"disambiguationData":[OSD([sQuery(id+"F8.wireOp",EDGE,"E18.bottom"),sQuery(id+"F8.wireOp",EDGE,"E18.right")])]})});
            var Q3;
            Q3=makeQuery(id+"F9.boolean.opBoolean","COPY",EDGE,{"derivedFrom":makeQuery(id+"F9.opRevolve","SWEPT_EDGE",EDGE,{"disambiguationData":[OSD([sQuery(id+"F8.wireOp",EDGE,"E18.top"),sQuery(id+"F8.wireOp",EDGE,"E18.right")])]})});
            chamfer(context, id + "F11", {"entities" : qUnion([Q0, Q1, Q2, Q3]), "width" : 1 * mm, "tangentPropagation" : true});
        }
        {
            var Q0;
            Q0=makeQuery(id+"F7.boolean.opBoolean","COPY",EDGE,{"derivedFrom":makeQuery(id+"F7.opExtrude","CAP_EDGE",EDGE,{"disambiguationData":[OSD([sQuery(id+"F4.wireOp",EDGE,"E15.1.0")])],"isStart":false})});
            var Q1;
            Q1=makeQuery(id+"F9.boolean.opBoolean","INTERSECT",EDGE,{"derivedFrom":[makeQuery(id+"F5.boolean.opBoolean","COPY",FACE,{"derivedFrom":makeQuery(id+"F5.opExtrude","SWEPT_FACE",FACE,{"disambiguationData":[OSD([sQuery(id+"F4.wireOp",EDGE,"E15.1.0")])]})}),makeQuery(id+"F9.opRevolve","SWEPT_FACE",FACE,{"disambiguationData":[OSD([sQuery(id+"F8.wireOp",EDGE,"E18.left")])]})]});
            var Q2;
            Q2=makeQuery(id+"F7.boolean.opBoolean","COPY",EDGE,{"derivedFrom":makeQuery(id+"F7.opExtrude","CAP_EDGE",EDGE,{"disambiguationData":[OSD([sQuery(id+"F4.wireOp",EDGE,"E14")])],"isStart":false})});
            var Q3;
            Q3=makeQuery(id+"F9.boolean.opBoolean","INTERSECT",EDGE,{"derivedFrom":[makeQuery(id+"F5.boolean.opBoolean","COPY",FACE,{"derivedFrom":makeQuery(id+"F5.opExtrude","SWEPT_FACE",FACE,{"disambiguationData":[OSD([sQuery(id+"F4.wireOp",EDGE,"E14")])]})}),makeQuery(id+"F9.opRevolve","SWEPT_FACE",FACE,{"disambiguationData":[OSD([sQuery(id+"F8.wireOp",EDGE,"E18.left")])]})]});
            var Q4;
            Q4=makeQuery(id+"F7.boolean.opBoolean","COPY",EDGE,{"derivedFrom":makeQuery(id+"F7.opExtrude","CAP_EDGE",EDGE,{"disambiguationData":[OSD([sQuery(id+"F4.wireOp",EDGE,"E15.6.0")])],"isStart":false})});
            var Q5;
            Q5=makeQuery(id+"F9.boolean.opBoolean","INTERSECT",EDGE,{"derivedFrom":[makeQuery(id+"F5.boolean.opBoolean","COPY",FACE,{"derivedFrom":makeQuery(id+"F5.opExtrude","SWEPT_FACE",FACE,{"disambiguationData":[OSD([sQuery(id+"F4.wireOp",EDGE,"E15.6.0")])]})}),makeQuery(id+"F9.opRevolve","SWEPT_FACE",FACE,{"disambiguationData":[OSD([sQuery(id+"F8.wireOp",EDGE,"E18.left")])]})]});
            var Q6;
            Q6=makeQuery(id+"F7.boolean.opBoolean","COPY",EDGE,{"derivedFrom":makeQuery(id+"F7.opExtrude","CAP_EDGE",EDGE,{"disambiguationData":[OSD([sQuery(id+"F4.wireOp",EDGE,"E15.5.0")])],"isStart":false})});
            var Q7;
            Q7=makeQuery(id+"F9.boolean.opBoolean","INTERSECT",EDGE,{"derivedFrom":[makeQuery(id+"F5.boolean.opBoolean","COPY",FACE,{"derivedFrom":makeQuery(id+"F5.opExtrude","SWEPT_FACE",FACE,{"disambiguationData":[OSD([sQuery(id+"F4.wireOp",EDGE,"E15.5.0")])]})}),makeQuery(id+"F9.opRevolve","SWEPT_FACE",FACE,{"disambiguationData":[OSD([sQuery(id+"F8.wireOp",EDGE,"E18.left")])]})]});
            var Q8;
            Q8=makeQuery(id+"F7.boolean.opBoolean","COPY",EDGE,{"derivedFrom":makeQuery(id+"F7.opExtrude","CAP_EDGE",EDGE,{"disambiguationData":[OSD([sQuery(id+"F4.wireOp",EDGE,"E15.4.0")])],"isStart":false})});
            var Q9;
            Q9=makeQuery(id+"F9.boolean.opBoolean","INTERSECT",EDGE,{"derivedFrom":[makeQuery(id+"F5.boolean.opBoolean","COPY",FACE,{"derivedFrom":makeQuery(id+"F5.opExtrude","SWEPT_FACE",FACE,{"disambiguationData":[OSD([sQuery(id+"F4.wireOp",EDGE,"E15.4.0")])]})}),makeQuery(id+"F9.opRevolve","SWEPT_FACE",FACE,{"disambiguationData":[OSD([sQuery(id+"F8.wireOp",EDGE,"E18.left")])]})]});
            var Q10;
            Q10=makeQuery(id+"F7.boolean.opBoolean","COPY",EDGE,{"derivedFrom":makeQuery(id+"F7.opExtrude","CAP_EDGE",EDGE,{"disambiguationData":[OSD([sQuery(id+"F4.wireOp",EDGE,"E15.3.0")])],"isStart":false})});
            var Q11;
            Q11=makeQuery(id+"F9.boolean.opBoolean","INTERSECT",EDGE,{"derivedFrom":[makeQuery(id+"F5.boolean.opBoolean","COPY",FACE,{"derivedFrom":makeQuery(id+"F5.opExtrude","SWEPT_FACE",FACE,{"disambiguationData":[OSD([sQuery(id+"F4.wireOp",EDGE,"E15.3.0")])]})}),makeQuery(id+"F9.opRevolve","SWEPT_FACE",FACE,{"disambiguationData":[OSD([sQuery(id+"F8.wireOp",EDGE,"E18.left")])]})]});
            var Q12;
            Q12=makeQuery(id+"F7.boolean.opBoolean","COPY",EDGE,{"derivedFrom":makeQuery(id+"F7.opExtrude","CAP_EDGE",EDGE,{"disambiguationData":[OSD([sQuery(id+"F4.wireOp",EDGE,"E15.2.0")])],"isStart":false})});
            var Q13;
            Q13=makeQuery(id+"F9.boolean.opBoolean","INTERSECT",EDGE,{"derivedFrom":[makeQuery(id+"F5.boolean.opBoolean","COPY",FACE,{"derivedFrom":makeQuery(id+"F5.opExtrude","SWEPT_FACE",FACE,{"disambiguationData":[OSD([sQuery(id+"F4.wireOp",EDGE,"E15.2.0")])]})}),makeQuery(id+"F9.opRevolve","SWEPT_FACE",FACE,{"disambiguationData":[OSD([sQuery(id+"F8.wireOp",EDGE,"E18.left")])]})]});
            chamfer(context, id + "F12", {"entities" : qUnion([Q0, Q1, Q2, Q3, Q4, Q5, Q6, Q7, Q8, Q9, Q10, Q11, Q12, Q13]), "width" : 2 * mm, "tangentPropagation" : true});
        }
    });
